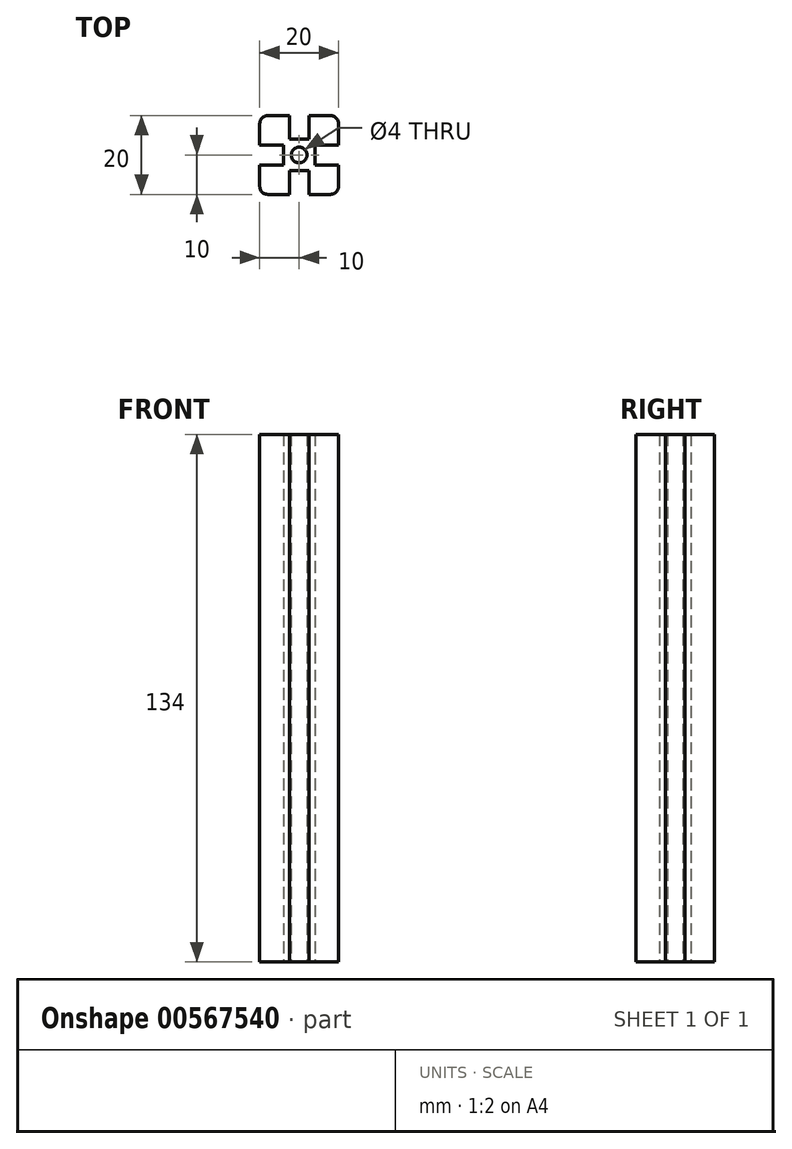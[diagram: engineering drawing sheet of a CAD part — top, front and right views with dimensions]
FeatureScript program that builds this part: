
annotation { "Feature Type Name" : "Feature", "Feature Type Description" : "" }
export const myFeature = defineFeature(function(context is Context, id is Id, definition is map)
    precondition{}
    {
        {
            var Q0;
            Q0=qCreatedBy(makeId("Top.planeOp"),FACE);
            var sketch = newSketch(context, id + "F0", { "sketchPlane" : qUnion([Q0])});
            skLineSegment(sketch, "E0", {"start": v(-4, 0) * mm, "end": v(-4, 2.5) * mm});
            skLineSegment(sketch, "E1", {"start": v(-4, 2.5) * mm, "end": v(-10, 2.5) * mm});
            skLineSegment(sketch, "E2", {"start": v(-10, 2.5) * mm, "end": v(-10, 10) * mm});
            skLineSegment(sketch, "E3", {"start": v(-10, 10) * mm, "end": v(-2.5, 10) * mm});
            skLineSegment(sketch, "E4", {"start": v(-2.5, 10) * mm, "end": v(-2.5, 4) * mm});
            skLineSegment(sketch, "E5", {"start": v(-2.5, 4) * mm, "end": v(0, 4) * mm});
            skLineSegment(sketch, "E6.MirrorCS", {"start": v(2.5, 4) * mm, "end": v(0, 4) * mm});
            skLineSegment(sketch, "E7.MirrorCS", {"start": v(4, 0) * mm, "end": v(4, 2.5) * mm});
            skLineSegment(sketch, "E8.MirrorCS", {"start": v(2.5, 10) * mm, "end": v(2.5, 4) * mm});
            skLineSegment(sketch, "E9.MirrorCS", {"start": v(10, 2.5) * mm, "end": v(10, 10) * mm});
            skLineSegment(sketch, "E10.MirrorCS", {"start": v(4, 2.5) * mm, "end": v(10, 2.5) * mm});
            skLineSegment(sketch, "E11.MirrorCS", {"start": v(10, 10) * mm, "end": v(2.5, 10) * mm});
            skLineSegment(sketch, "E12.MirrorCS", {"start": v(10, -10) * mm, "end": v(2.5, -10) * mm});
            skLineSegment(sketch, "E13.MirrorCS", {"start": v(4, -2.5) * mm, "end": v(10, -2.5) * mm});
            skLineSegment(sketch, "E14.MirrorCS", {"start": v(10, -2.5) * mm, "end": v(10, -10) * mm});
            skLineSegment(sketch, "E15.MirrorCS", {"start": v(2.5, -10) * mm, "end": v(2.5, -4) * mm});
            skLineSegment(sketch, "E16.MirrorCS", {"start": v(4, 0) * mm, "end": v(4, -2.5) * mm});
            skLineSegment(sketch, "E17.MirrorCS", {"start": v(2.5, -4) * mm, "end": v(0, -4) * mm});
            skLineSegment(sketch, "E18.MirrorCS", {"start": v(-10, -2.5) * mm, "end": v(-10, -10) * mm});
            skLineSegment(sketch, "E19.MirrorCS", {"start": v(-4, -2.5) * mm, "end": v(-10, -2.5) * mm});
            skLineSegment(sketch, "E20.MirrorCS", {"start": v(-4, 0) * mm, "end": v(-4, -2.5) * mm});
            skLineSegment(sketch, "E21.MirrorCS", {"start": v(-2.5, -10) * mm, "end": v(-2.5, -4) * mm});
            skLineSegment(sketch, "E22.MirrorCS", {"start": v(-10, -10) * mm, "end": v(-2.5, -10) * mm});
            skLineSegment(sketch, "E23.MirrorCS", {"start": v(-2.5, -4) * mm, "end": v(0, -4) * mm});
            skCircle(sketch, "E24", {"center": v(0, 0) * mm, "radius": 2 * mm});
            skSolve(sketch);
        }
        {
            var Q0;
            Q0 = qSketchRegion(id + "F0", true);
            extrude(context, id + "F1", {"entities" : qUnion([Q0]), "depth" : 134 * mm, "offsetDistance" : 25 * mm});
        }
        {
            var Q0;
            Q0=makeQuery(id+"F1.opExtrude","SWEPT_EDGE",EDGE,{"disambiguationData":[OSD([sQuery(id+"F0.wireOp",EDGE,"E12.MirrorCS"),sQuery(id+"F0.wireOp",EDGE,"E14.MirrorCS")])]});
            var Q1;
            Q1=makeQuery(id+"F1.opExtrude","SWEPT_EDGE",EDGE,{"disambiguationData":[OSD([sQuery(id+"F0.wireOp",EDGE,"E18.MirrorCS"),sQuery(id+"F0.wireOp",EDGE,"E22.MirrorCS")])]});
            var Q2;
            Q2=makeQuery(id+"F1.opExtrude","SWEPT_EDGE",EDGE,{"disambiguationData":[OSD([sQuery(id+"F0.wireOp",EDGE,"E2"),sQuery(id+"F0.wireOp",EDGE,"E3")])]});
            var Q3;
            Q3=makeQuery(id+"F1.opExtrude","SWEPT_EDGE",EDGE,{"disambiguationData":[OSD([sQuery(id+"F0.wireOp",EDGE,"E9.MirrorCS"),sQuery(id+"F0.wireOp",EDGE,"E11.MirrorCS")])]});
            fillet(context, id + "F2", {"entities" : qUnion([Q0, Q1, Q2, Q3]), "radius" : 2 * mm, "tangentPropagation" : true, "allowEdgeOverflow" : false});
        }
    });
